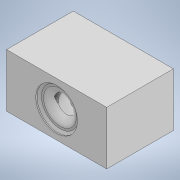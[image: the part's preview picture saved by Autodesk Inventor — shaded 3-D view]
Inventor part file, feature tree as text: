
AUTODESK INVENTOR PART (.ipt)
format: ipt  version: 2022 (Build 260153000, 153)  size: 781,312 bytes
history: native  units: mm
features: extrude x2, delete_face x2, sketch x2, boolean_combine x1
ambient origin geometry x8: Origin, YZ Plane, XZ Plane, XY Plane, X Axis, Y Axis, Z Axis, Center Point
bodies: Solid4 (feature_tree), Solid1 (feature_tree), Solid6 (feature_tree)
feature tree (7):
  extrude  "Extrusion4"  Depth=8.0mm
  boolean_combine  "Combine3"
  extrude  "Extrusion6"  Depth=20.0mm
  delete_face  "Delete Face6"
  delete_face  "Delete Face7"
  sketch  "Sketch4"  dims[d21=8.0mm d22=8.0mm]
  sketch  "Sketch7"  dims[d23=15.0mm d24=30.0mm d25=20.0mm d26=0.0mm d31=6.0mm d32=1.0mm d33=0.0mm]
